# Revit family: Gira_015430
name_source: partatom
category: Electrical Fixtures
revit_build: Autodesk Revit 2017 (Build: 20160225_1515(x64)
units: mm (PartAtom-declared; Revit-internal decimal feet)

## family parameters
Cut with Voids When Loaded = No
Host = Face
Maintain Annotation Orientation = No
Part Type = Normal
Room Calculation Point = No
Round Connector Dimension = Use Diameter
Shared = No

## types (1)
- Blind sw./btn 1-p in.sp. WP SM grey
    Assembly arrangement = Basic element with complete housing
    BIM = https://media.live.bim.site
    BIMSITE_PRODUCT_ID = dec14956e846116d78083a73c1339239001a9d03
    Colour = Grey
    Cost = 0 $
    Default Elevation = 1219 mm
    Description = Blind 1-p WP SM GY Blind button or switch 1-pole 10 AX 250 V~ with inscription space Group button switch grey Notes : - Button function upon rotation of the toggle switch. After removing the brass locking mechanism, button function upon slight rotation of the knob. When fully rotating the knob, the switch engages.
    Electrical and mechanical locking = No
    Electronic controllable = No
    GTIN = 4010337154303
    HAN = 015430
    Halogen free = No
    HeinzeBIM = https://www.heinze.de
    Label space/information surface YesNo = Yes
    Manufacturer = Gira
    Material = plastic
    Material quality = Thermoplastic
    Mechanical controllable = Yes
    Method of operation = Turn button
    Model = 1-pole switch
    Nominal voltage [Volt] Number = 250
    Number of modules (module system) = 1
    Rated current [Ampere] = 10
    Suitable for degree of protection (IP) = IP44
    Surface protection = Sonstige (*de-DE)
    Type of fastening = Mounting with screw
    URL = https://www.gira.de

## geometry (parser evidence)
native form markers: Blend x2, Sweep x14
no freeform markers — native parametric forms only
